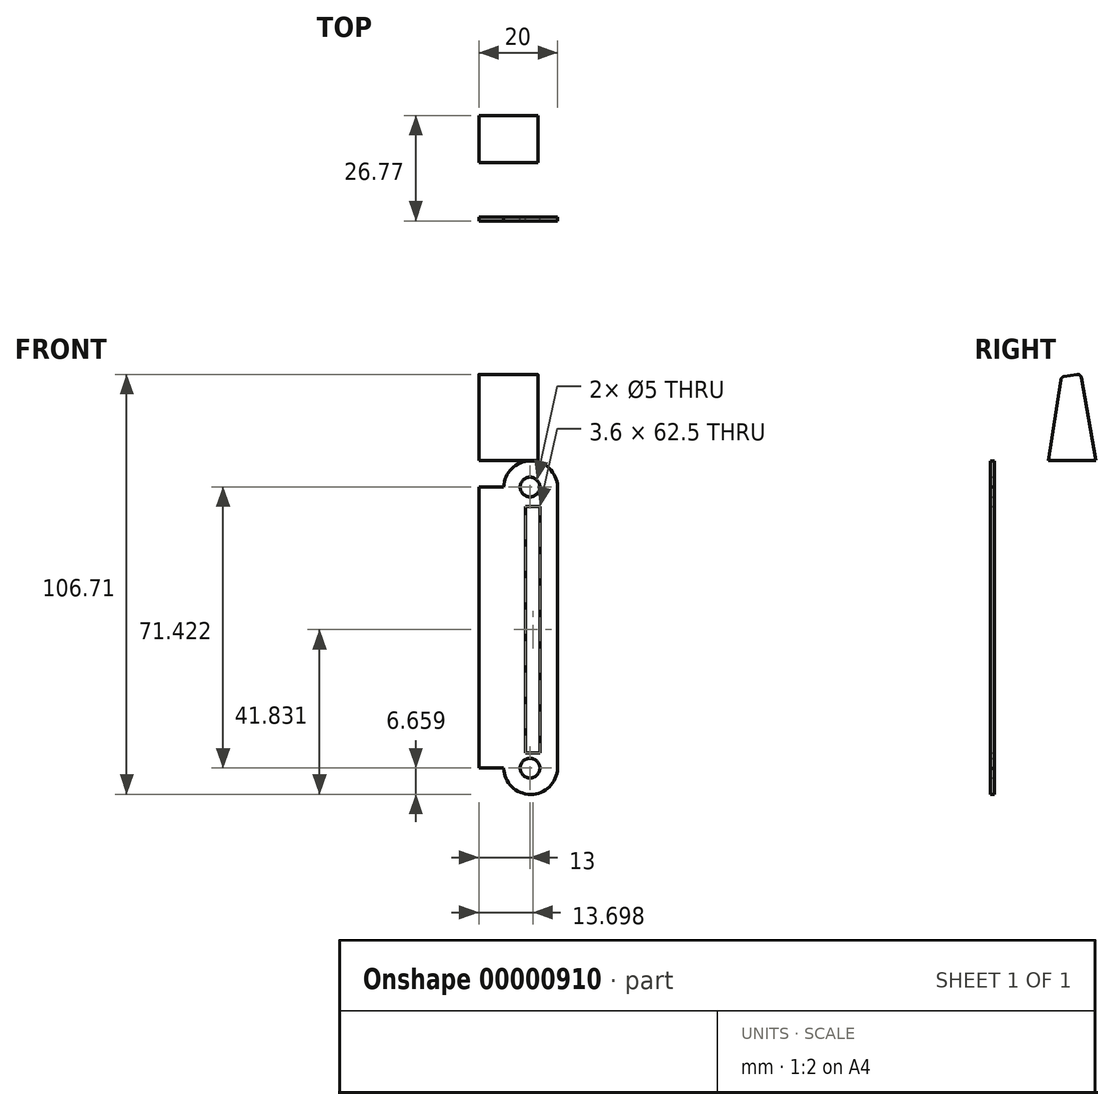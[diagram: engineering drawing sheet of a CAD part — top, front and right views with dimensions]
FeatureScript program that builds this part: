
annotation { "Feature Type Name" : "Feature", "Feature Type Description" : "" }
export const myFeature = defineFeature(function(context is Context, id is Id, definition is map)
    precondition{}
    {
        {
            var Q0;
            Q0=qCreatedBy(makeId("Front.planeOp"),FACE);
            var sketch = newSketch(context, id + "F0", { "sketchPlane" : qUnion([Q0])});
            skLineSegment(sketch, "E0.left", {"start": v(0, -6.79) * mm, "end": v(0, -78.21) * mm});
            skLineSegment(sketch, "E0.right", {"start": v(20, -6.77) * mm, "end": v(20, -78.23) * mm});
            skLineSegment(sketch, "E1.bottom", {"start": v(11.9, -11.79) * mm, "end": v(15.5, -11.79) * mm});
            skLineSegment(sketch, "E1.top", {"start": v(11.9, -74.29) * mm, "end": v(15.5, -74.29) * mm});
            skLineSegment(sketch, "E1.left", {"start": v(11.9, -11.79) * mm, "end": v(11.9, -74.29) * mm});
            skLineSegment(sketch, "E1.right", {"start": v(15.5, -11.79) * mm, "end": v(15.5, -74.29) * mm});
            skCircle(sketch, "E2", {"center": v(13, -6.79) * mm, "radius": 2.5 * mm});
            skLineSegment(sketch, "E3", {"start": v(0, -6.79) * mm, "end": v(6.3, -6.79) * mm});
            skArc(sketch, "E4", {"start": v(20, -6.77) * mm, "mid": v(13.14, -0.13) * mm, "end": v(6.3, -6.79) * mm});
            skCircle(sketch, "E5.0.MirrorC", {"center": v(13, -78.21) * mm, "radius": 2.5 * mm});
            skArc(sketch, "E6.0.MirrorCS", {"start": v(20, -78.23) * mm, "mid": v(13.14, -84.87) * mm, "end": v(6.3, -78.21) * mm});
            skLineSegment(sketch, "E7.0.MirrorCS", {"start": v(0, -78.21) * mm, "end": v(6.3, -78.21) * mm});
            skSolve(sketch);
        }
        {
            var Q0;
            Q0=makeQuery(id+"F0.imprint","IMPRINT",FACE,{"disambiguationData":[TD([[makeQuery(id+"F0.imprint","IMPRINT",EDGE,{"derivedFrom":sQuery(id+"F0.wireOp",EDGE,"E0.left")}),1.0]])]});
            extrude(context, id + "F1", {"entities" : qUnion([Q0]), "depth" : 1 * mm});
        }
        {
            var Q0;
            Q0=makeQuery(id+"F1.opExtrude","SWEPT_BODY",BODY,{"disambiguationData":[OSD([sQuery(id+"F0.wireOp",EDGE,"E0.left"),sQuery(id+"F0.wireOp",EDGE,"E0.right"),sQuery(id+"F0.wireOp",EDGE,"E1.bottom"),sQuery(id+"F0.wireOp",EDGE,"E1.top"),sQuery(id+"F0.wireOp",EDGE,"E1.left"),sQuery(id+"F0.wireOp",EDGE,"E1.right"),sQuery(id+"F0.wireOp",EDGE,"E2"),sQuery(id+"F0.wireOp",EDGE,"E3"),sQuery(id+"F0.wireOp",EDGE,"E4"),sQuery(id+"F0.wireOp",EDGE,"E5.0.MirrorC"),sQuery(id+"F0.wireOp",EDGE,"E6.0.MirrorCS"),sQuery(id+"F0.wireOp",EDGE,"E7.0.MirrorCS")])]});
            transform(context, id + "F2", {"entities" : qUnion([Q0]), "transformType" : TransformType.COPY, "oppositeX" : false, "oppositeY" : false, "oppositeZ" : false});
        }
        {
            var Q0;
            Q0=qCreatedBy(makeId("Right.planeOp"),FACE);
            var sketch = newSketch(context, id + "F3", { "sketchPlane" : qUnion([Q0])});
            skLineSegment(sketch, "E8", {"start": v(13.77, 0) * mm, "end": v(25.77, 0) * mm});
            skLineSegment(sketch, "E9", {"start": v(25.77, 0) * mm, "end": v(22.12, 21.01) * mm});
            skLineSegment(sketch, "E10", {"start": v(20.96, 21.83) * mm, "end": v(17.73, 21.27) * mm});
            skLineSegment(sketch, "E11", {"start": v(16.91, 20.43) * mm, "end": v(13.77, 0) * mm});
            skPoint(sketch, "E12.visualSharp", {"position": v(17.02, 21.14) * mm});
            skArc(sketch, "E12.filletArc", {"start": v(17.73, 21.27) * mm, "mid": v(17.19, 20.98) * mm, "end": v(16.91, 20.43) * mm});
            skPoint(sketch, "E13.visualSharp", {"position": v(21.95, 22) * mm});
            skArc(sketch, "E13.filletArc", {"start": v(22.12, 21.01) * mm, "mid": v(21.7, 21.66) * mm, "end": v(20.96, 21.83) * mm});
            skSolve(sketch);
        }
        {
            var Q0;
            Q0=makeQuery(id+"F3.imprint","IMPRINT",FACE,{"disambiguationData":[TD([[makeQuery(id+"F3.imprint","IMPRINT",EDGE,{"derivedFrom":sQuery(id+"F3.wireOp",EDGE,"E8")}),1.0]])]});
            extrude(context, id + "F4", {"entities" : qUnion([Q0]), "depth" : 15 * mm});
        }
        {
            var Q0;
            Q0=makeQuery(id+"F2.opPattern","COPY",BODY,{"derivedFrom":makeQuery(id+"F1.opExtrude","SWEPT_BODY",BODY,{"disambiguationData":[OSD([sQuery(id+"F0.wireOp",EDGE,"E0.left"),sQuery(id+"F0.wireOp",EDGE,"E0.right"),sQuery(id+"F0.wireOp",EDGE,"E1.bottom"),sQuery(id+"F0.wireOp",EDGE,"E1.top"),sQuery(id+"F0.wireOp",EDGE,"E1.left"),sQuery(id+"F0.wireOp",EDGE,"E1.right"),sQuery(id+"F0.wireOp",EDGE,"E2"),sQuery(id+"F0.wireOp",EDGE,"E3"),sQuery(id+"F0.wireOp",EDGE,"E4"),sQuery(id+"F0.wireOp",EDGE,"E5.0.MirrorC"),sQuery(id+"F0.wireOp",EDGE,"E6.0.MirrorCS"),sQuery(id+"F0.wireOp",EDGE,"E7.0.MirrorCS")])]}),"instanceName":"1"});
            deleteBodies(context, id + "F5", {"entities" : qUnion([Q0])});
        }
    });
